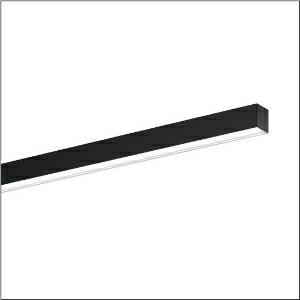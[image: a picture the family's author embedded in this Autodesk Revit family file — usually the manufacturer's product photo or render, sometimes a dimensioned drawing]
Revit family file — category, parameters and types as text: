
# Revit family: silica_r__21_51mx23dc3abb_3531
name_source: partatom
category: Lighting Fixtures
units: mm (PartAtom-declared; Revit-internal decimal feet)

## family parameters
Cut with Voids When Loaded = No
Host = Face
Light Source = No
Part Type = Normal
Room Calculation Point = No
Round Connector Dimension = Use Diameter
Shared = No

## types (1)
- --- (1 x LED, 8200 lm, 62.2 W, 3000K)
    Apparent Load = 62 VA
    CIE Flux Codes = 78 96 99 100 100
    Color Rendering = 80
    Color Temperature = 3000K
    Default Elevation = 1800 mm
    Description = Silica® 21, office luminaire, primary optical cover: prismatic diffuser, of PMMA, CAT 2 (L<= 3000cd/m²), light emission: direct distribution, primary light characteristic: symmetric, installation type: surface-mounted, LED, rated luminous flux: 8.200lm, luminous efficacy: 132lm/W, light colour: 830, colour temperature: 3000K, control gear: DALI 2, with terminal, 3+2-pole, max. 2.5mm², mains connection: 220..240V, AC, 50/60Hz, rated input power: 62.2W, luminaire housing, of aluminium, matt jet black (RAL 9005), length: 3.004mm, width: 53mm, height: 53mm, protection rating (complete): IP20, insulation class (complete): insulation class I (protective earthing), certification: CE, permissible operating ambient temperature: 0..+35°C, standard: EN 50419, packaging unit: 1 piece
    Height = 53 mm
    Lamp = 1 x LED
    Lamp Light Flux = 8200 lm
    Lamp Power = 62.2 W
    Lamp count = 1
    Length = 3004 mm
    Luminous efficacy = 132 lm/W
    Manufacturer = Siteco
    ModVariant = No
    Model = 51MX23DC3ABB
    Mounting Place = Ceiling
    Mounting Type = Surface mounted
    Number of Poles = 1
    OnlyDefault = Yes
    Power Factor = 1
    Product Name = Silica® 21
    Product group = office luminaire | ceiling mounted
    ProductGroupID = 302
    Protection Class = Protection class I
    Protection Degree = IP 20
    RLX_Detail_Level = 1
    RLX_Emergency_Light_Flux = 0 lm
    RLX_Emergency_Type = 0
    RLX_Emergency_Type_DB = No
    RlxData = <blob elided: 23685 chars, md5=a00c0877>
    Socket = socket
    Standby Power = 0 W
    System Light Flux = 8200 lm
    System Power = 62 W
    Type Comments = factory setting: luminous flux: 100 % | dim-lin: 254 | 345 mA
    Type Image = l_1335925.jpg
    URL = http://relux.com
    VarID = @adj_119296
    Voltage = 0 V
    Weight = 0.00 kg
    Width = 53 mm

## geometry (parser evidence)
native form markers: Blend x4, Sweep x12
no freeform markers — native parametric forms only
